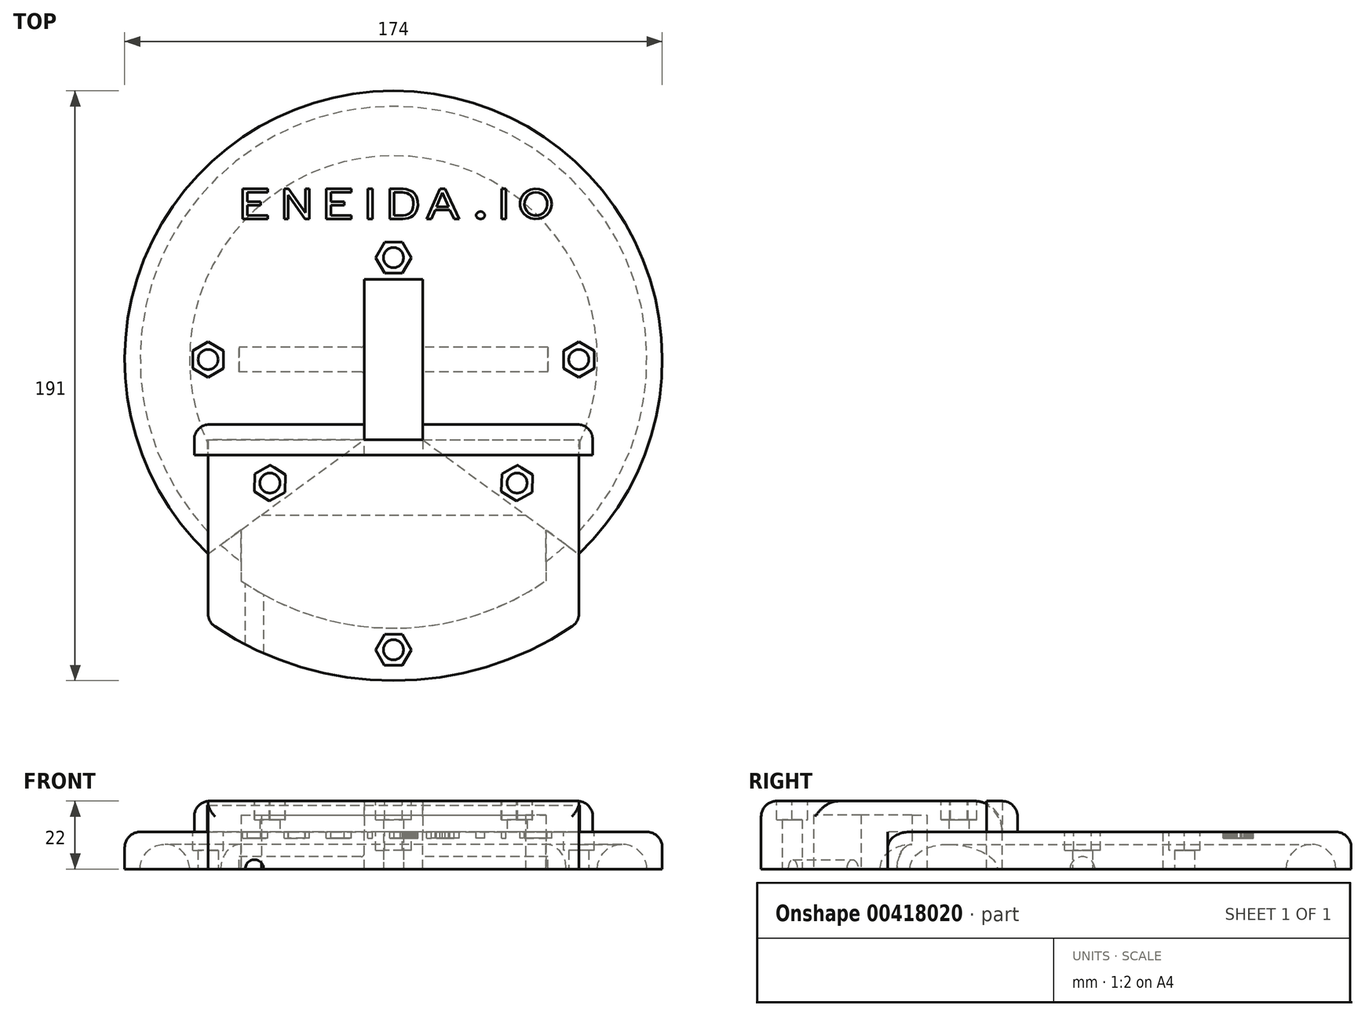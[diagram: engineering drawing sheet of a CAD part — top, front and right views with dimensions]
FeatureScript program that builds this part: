
annotation { "Feature Type Name" : "Feature", "Feature Type Description" : "" }
export const myFeature = defineFeature(function(context is Context, id is Id, definition is map)
    precondition{}
    {
        {
            var Q0;
            Q0=qCreatedBy(makeId("Top.planeOp"),FACE);
            var sketch = newSketch(context, id + "F0", { "sketchPlane" : qUnion([Q0])});
            skCircle(sketch, "E0", {"center": v(0, 0) * mm, "radius": 74 * mm});
            skCircle(sketch, "E1", {"center": v(0, 0) * mm, "radius": 87 * mm});
            skLineSegment(sketch, "E2", {"start": v(9.5, 26) * mm, "end": v(-9.5, 26) * mm});
            skLineSegment(sketch, "E3", {"start": v(-9.5, 26) * mm, "end": v(-9.5, -26) * mm});
            skLineSegment(sketch, "E4", {"start": v(9.5, 26) * mm, "end": v(9.5, -26) * mm});
            skCircle(sketch, "E5", {"center": v(-40, -40) * mm, "radius": 3.25 * mm});
            skCircle(sketch, "E6", {"center": v(-40, 40) * mm, "radius": 3.25 * mm});
            skCircle(sketch, "E7", {"center": v(40, 40) * mm, "radius": 3.25 * mm});
            skCircle(sketch, "E8", {"center": v(40, -40) * mm, "radius": 3.25 * mm});
            skPoint(sketch, "E9.endSnap0", {"position": v(0, 26) * mm});
            skCircle(sketch, "E10", {"center": v(0, 33) * mm, "radius": 3.25 * mm});
            skCircle(sketch, "E11", {"center": v(-60, 0) * mm, "radius": 3.25 * mm});
            skCircle(sketch, "E12", {"center": v(60, 0) * mm, "radius": 3.25 * mm});
            skLineSegment(sketch, "E13", {"start": v(0, 0) * mm, "end": v(-40, 0) * mm});
            skPoint(sketch, "E13.endSnap0", {"position": v(-9.5, 0) * mm});
            skLineSegment(sketch, "E14", {"start": v(-60, 0) * mm, "end": v(-60, -63) * mm});
            skLineSegment(sketch, "E15", {"start": v(-60, -63) * mm, "end": v(-9.5, -26) * mm});
            skLineSegment(sketch, "E16", {"start": v(60, 0) * mm, "end": v(60, -63) * mm});
            skLineSegment(sketch, "E17", {"start": v(60, -63) * mm, "end": v(9.5, -26) * mm});
            skLineSegment(sketch, "E18", {"start": v(-9.5, -26) * mm, "end": v(9.5, -26) * mm});
            skLineSegment(sketch, "E19", {"start": v(-9.5, -26) * mm, "end": v(-60, -26) * mm});
            skLineSegment(sketch, "E20", {"start": v(9.5, -26) * mm, "end": v(60, -26) * mm});
            skLineSegment(sketch, "E21", {"start": v(-42.7, -50.33) * mm, "end": v(42.7, -50.33) * mm});
            skLineSegment(sketch, "E22", {"start": v(-60, -63) * mm, "end": v(-60, -98) * mm});
            skCircle(sketch, "E23", {"center": v(0, 0) * mm, "radius": 114.9 * mm});
            skLineSegment(sketch, "E24", {"start": v(60, -63) * mm, "end": v(60, -98) * mm});
            skCircle(sketch, "E25", {"center": v(0, 0) * mm, "radius": 91 * mm});
            skLineSegment(sketch, "E26", {"start": v(-49.32, -55.17) * mm, "end": v(-49.32, -76.48) * mm});
            skLineSegment(sketch, "E27", {"start": v(49.32, -55.17) * mm, "end": v(49.32, -76.48) * mm});
            skLineSegment(sketch, "E28", {"start": v(0, 0) * mm, "end": v(0, -94) * mm});
            skCircle(sketch, "E29", {"center": v(0, -94) * mm, "radius": 3.25 * mm});
            skCircle(sketch, "E30", {"center": v(0, 0) * mm, "radius": 104 * mm});
            skLineSegment(sketch, "E31", {"start": v(-49.32, -76.48) * mm, "end": v(49.32, -76.48) * mm});
            skSolve(sketch);
        }
        {
            var Q0;
            {var subQ0=sQuery(id+"F0.wireOp",EDGE,"TgP18rpg-E85a-n0eO-8987-ISkSi9N6DLmr");var subQ1=sQuery(id+"F0.wireOp",EDGE,"E0");var subQ2=makeQuery(id+"F0.imprint","INTERSECT",VERTEX,{"derivedFrom":[subQ1,subQ0]});Q0=makeQuery(id+"F0.imprint","IMPRINT",FACE,{"disambiguationData":[TD([[makeQuery(id+"F0.imprint","IMPRINT",EDGE,{"disambiguationData":[TD([[subQ2,1.0]])],"derivedFrom":subQ1}),-1.0]])]});}
            var Q1;
            Q1=makeQuery(id+"F0.imprint","IMPRINT",FACE,{"disambiguationData":[TD([[makeQuery(id+"F0.imprint","IMPRINT",EDGE,{"derivedFrom":sQuery(id+"F0.wireOp",EDGE,"E2")}),-1.0]])]});
            var Q2;
            {var subQ0=sQuery(id+"F0.wireOp",EDGE,"RmQZDrMv-17gZ-rr8W-YuSi-1pivtKFGjAAM.left");var subQ1=sQuery(id+"F0.wireOp",EDGE,"RmQZDrMv-17gZ-rr8W-YuSi-1pivtKFGjAAM.bottom");var subQ2=makeQuery(id+"F0.imprint","INTERSECT",VERTEX,{"derivedFrom":[subQ1,subQ0]});Q2=makeQuery(id+"F0.imprint","IMPRINT",FACE,{"disambiguationData":[TD([[makeQuery(id+"F0.imprint","IMPRINT",EDGE,{"disambiguationData":[TD([[subQ2,-1.0]])],"derivedFrom":subQ1}),-1.0]])]});}
            var Q3;
            {var subQ0=sQuery(id+"F0.wireOp",EDGE,"RmQZDrMv-17gZ-rr8W-YuSi-1pivtKFGjAAM.left");var subQ1=sQuery(id+"F0.wireOp",EDGE,"RmQZDrMv-17gZ-rr8W-YuSi-1pivtKFGjAAM.bottom");var subQ2=makeQuery(id+"F0.imprint","INTERSECT",VERTEX,{"derivedFrom":[subQ1,subQ0]});Q3=makeQuery(id+"F0.imprint","IMPRINT",FACE,{"disambiguationData":[TD([[makeQuery(id+"F0.imprint","IMPRINT",EDGE,{"disambiguationData":[TD([[subQ2,-1.0]])],"derivedFrom":subQ1}),1.0]])]});}
            var Q4;
            {var subQ0=sQuery(id+"F0.wireOp",EDGE,"RmQZDrMv-17gZ-rr8W-YuSi-1pivtKFGjAAM.left");var subQ1=sQuery(id+"F0.wireOp",EDGE,"RmQZDrMv-17gZ-rr8W-YuSi-1pivtKFGjAAM.top");var subQ2=makeQuery(id+"F0.imprint","INTERSECT",VERTEX,{"derivedFrom":[subQ1,subQ0]});Q4=makeQuery(id+"F0.imprint","IMPRINT",FACE,{"disambiguationData":[TD([[makeQuery(id+"F0.imprint","IMPRINT",EDGE,{"disambiguationData":[TD([[subQ2,-1.0]])],"derivedFrom":subQ1}),1.0]])]});}
            var Q5;
            {var subQ0=sQuery(id+"F0.wireOp",EDGE,"RmQZDrMv-17gZ-rr8W-YuSi-1pivtKFGjAAM.left");var subQ1=sQuery(id+"F0.wireOp",EDGE,"RmQZDrMv-17gZ-rr8W-YuSi-1pivtKFGjAAM.top");var subQ2=makeQuery(id+"F0.imprint","INTERSECT",VERTEX,{"derivedFrom":[subQ1,subQ0]});Q5=makeQuery(id+"F0.imprint","IMPRINT",FACE,{"disambiguationData":[TD([[makeQuery(id+"F0.imprint","IMPRINT",EDGE,{"disambiguationData":[TD([[subQ2,-1.0]])],"derivedFrom":subQ1}),-1.0]])]});}
            var Q6;
            {var subQ0=sQuery(id+"F0.wireOp",EDGE,"RmQZDrMv-17gZ-rr8W-YuSi-1pivtKFGjAAM.right");var subQ1=sQuery(id+"F0.wireOp",EDGE,"RmQZDrMv-17gZ-rr8W-YuSi-1pivtKFGjAAM.top");var subQ2=makeQuery(id+"F0.imprint","INTERSECT",VERTEX,{"derivedFrom":[subQ1,subQ0]});Q6=makeQuery(id+"F0.imprint","IMPRINT",FACE,{"disambiguationData":[TD([[makeQuery(id+"F0.imprint","IMPRINT",EDGE,{"disambiguationData":[TD([[subQ2,1.0]])],"derivedFrom":subQ1}),1.0]])]});}
            var Q7;
            {var subQ0=sQuery(id+"F0.wireOp",EDGE,"RmQZDrMv-17gZ-rr8W-YuSi-1pivtKFGjAAM.right");var subQ1=sQuery(id+"F0.wireOp",EDGE,"RmQZDrMv-17gZ-rr8W-YuSi-1pivtKFGjAAM.top");var subQ2=makeQuery(id+"F0.imprint","INTERSECT",VERTEX,{"derivedFrom":[subQ1,subQ0]});Q7=makeQuery(id+"F0.imprint","IMPRINT",FACE,{"disambiguationData":[TD([[makeQuery(id+"F0.imprint","IMPRINT",EDGE,{"disambiguationData":[TD([[subQ2,1.0]])],"derivedFrom":subQ1}),-1.0]])]});}
            var Q8;
            {var subQ0=sQuery(id+"F0.wireOp",EDGE,"RmQZDrMv-17gZ-rr8W-YuSi-1pivtKFGjAAM.right");var subQ1=sQuery(id+"F0.wireOp",EDGE,"RmQZDrMv-17gZ-rr8W-YuSi-1pivtKFGjAAM.bottom");var subQ2=makeQuery(id+"F0.imprint","INTERSECT",VERTEX,{"derivedFrom":[subQ1,subQ0]});Q8=makeQuery(id+"F0.imprint","IMPRINT",FACE,{"disambiguationData":[TD([[makeQuery(id+"F0.imprint","IMPRINT",EDGE,{"disambiguationData":[TD([[subQ2,1.0]])],"derivedFrom":subQ1}),1.0]])]});}
            var Q9;
            {var subQ0=sQuery(id+"F0.wireOp",EDGE,"RmQZDrMv-17gZ-rr8W-YuSi-1pivtKFGjAAM.right");var subQ1=sQuery(id+"F0.wireOp",EDGE,"RmQZDrMv-17gZ-rr8W-YuSi-1pivtKFGjAAM.bottom");var subQ2=makeQuery(id+"F0.imprint","INTERSECT",VERTEX,{"derivedFrom":[subQ1,subQ0]});Q9=makeQuery(id+"F0.imprint","IMPRINT",FACE,{"disambiguationData":[TD([[makeQuery(id+"F0.imprint","IMPRINT",EDGE,{"disambiguationData":[TD([[subQ2,1.0]])],"derivedFrom":subQ1}),-1.0]])]});}
            var Q10;
            Q10=makeQuery(id+"F0.imprint","IMPRINT",FACE,{"disambiguationData":[TD([[makeQuery(id+"F0.imprint","IMPRINT",EDGE,{"derivedFrom":sQuery(id+"F0.wireOp",EDGE,"E7")}),1.0]])]});
            var Q11;
            Q11=makeQuery(id+"F0.imprint","IMPRINT",FACE,{"disambiguationData":[TD([[makeQuery(id+"F0.imprint","IMPRINT",EDGE,{"derivedFrom":sQuery(id+"F0.wireOp",EDGE,"E6")}),1.0]])]});
            var Q12;
            Q12=makeQuery(id+"F0.imprint","IMPRINT",FACE,{"disambiguationData":[TD([[makeQuery(id+"F0.imprint","IMPRINT",EDGE,{"derivedFrom":sQuery(id+"F0.wireOp",EDGE,"E5")}),1.0]])]});
            var Q13;
            Q13=makeQuery(id+"F0.imprint","IMPRINT",FACE,{"disambiguationData":[TD([[makeQuery(id+"F0.imprint","IMPRINT",EDGE,{"derivedFrom":sQuery(id+"F0.wireOp",EDGE,"E8")}),1.0]])]});
            var Q14;
            Q14=makeQuery(id+"F0.imprint","IMPRINT",FACE,{"disambiguationData":[TD([[makeQuery(id+"F0.imprint","IMPRINT",EDGE,{"derivedFrom":sQuery(id+"F0.wireOp",EDGE,"E8")}),-1.0]])]});
            var Q15;
            {var subQ0=sQuery(id+"F0.wireOp",EDGE,"E14");var subQ1=sQuery(id+"F0.wireOp",EDGE,"E0");var subQ2=makeQuery(id+"F0.imprint","INTERSECT",VERTEX,{"derivedFrom":[subQ1,subQ0]});Q15=makeQuery(id+"F0.imprint","IMPRINT",FACE,{"disambiguationData":[TD([[makeQuery(id+"F0.imprint","IMPRINT",EDGE,{"disambiguationData":[TD([[subQ2,1.0]])],"derivedFrom":subQ1}),-1.0]])]});}
            var Q16;
            Q16=makeQuery(id+"F0.imprint","IMPRINT",FACE,{"disambiguationData":[TD([[makeQuery(id+"F0.imprint","IMPRINT",EDGE,{"derivedFrom":sQuery(id+"F0.wireOp",EDGE,"E5")}),-1.0]])]});
            var Q17;
            {var subQ1=sQuery(id+"F0.wireOp",EDGE,"E0");var subQ3=sQuery(id+"F0.wireOp",EDGE,"E14");var subQ4=makeQuery(id+"F0.imprint","INTERSECT",VERTEX,{"derivedFrom":[subQ1,subQ3]});Q17=makeQuery(id+"F0.imprint","IMPRINT",FACE,{"disambiguationData":[TD([[makeQuery(id+"F0.imprint","IMPRINT",EDGE,{"disambiguationData":[TD([[subQ4,-1.0]])],"derivedFrom":subQ1}),-1.0]])]});}
            extrude(context, id + "F1", {"entities" : qUnion([Q0, Q1, Q2, Q3, Q4, Q5, Q6, Q7, Q8, Q9, Q10, Q11, Q12, Q13, Q14, Q15, Q16, Q17]), "depth" : 12 * mm});
        }
        {
            var Q0;
            Q0=makeQuery(id+"F0.imprint","IMPRINT",FACE,{"disambiguationData":[TD([[makeQuery(id+"F0.imprint","IMPRINT",EDGE,{"derivedFrom":sQuery(id+"F0.wireOp",EDGE,"E2")}),1.0]])]});
            var Q1;
            {var subQ0=sQuery(id+"F0.wireOp",EDGE,"TgP18rpg-E85a-n0eO-8987-ISkSi9N6DLmr");var subQ1=sQuery(id+"F0.wireOp",EDGE,"E0");var subQ2=makeQuery(id+"F0.imprint","INTERSECT",VERTEX,{"derivedFrom":[subQ1,subQ0]});Q1=makeQuery(id+"F0.imprint","IMPRINT",FACE,{"disambiguationData":[TD([[makeQuery(id+"F0.imprint","IMPRINT",EDGE,{"disambiguationData":[TD([[subQ2,-1.0]])],"derivedFrom":subQ1}),-1.0]])]});}
            extrude(context, id + "F2", {"entities" : qUnion([Q0, Q1]), "operationType" : NewBodyOperationType.REMOVE, "oppositeDirection" : true, "depth" : 12 * mm});
        }
        {
            var Q0;
            Q0=makeQuery(id+"F1.opExtrude","CAP_FACE",FACE,{"disambiguationData":[OSD([sQuery(id+"F0.wireOp",EDGE,"E1"),sQuery(id+"F0.wireOp",EDGE,"E2"),sQuery(id+"F0.wireOp",EDGE,"E3"),sQuery(id+"F0.wireOp",EDGE,"E4"),sQuery(id+"F0.wireOp",EDGE,"TgP18rpg-E85a-n0eO-8987-ISkSi9N6DLmr"),sQuery(id+"F0.wireOp",EDGE,"ek1SPQXI-mJC3-1PxT-7uTG-ug6Pz7o93UjJ"),sQuery(id+"F0.wireOp",EDGE,"E10"),sQuery(id+"F0.wireOp",EDGE,"E11"),sQuery(id+"F0.wireOp",EDGE,"E12")])],"isStart":false});
            cPlane(context, id + "F3", {"entities" : qUnion([Q0]), "cplaneType" : CPlaneType.OFFSET, "offset" : 0 * mm, "width" : 150 * mm, "height" : 150 * mm});
        }
        {
            var Q0;
            Q0=qCreatedBy(id+"F3.planeOp",FACE);
            var sketch = newSketch(context, id + "F4", { "sketchPlane" : qUnion([Q0])});
            skLineSegment(sketch, "E32", {"start": v(0, 0) * mm, "end": v(0, 33) * mm});
            skLineSegment(sketch, "E33.0", {"start": v(2.89, 28) * mm, "end": v(-2.89, 28) * mm});
            skLineSegment(sketch, "E33.1", {"start": v(-2.89, 28) * mm, "end": v(-5.77, 33) * mm});
            skLineSegment(sketch, "E33.2", {"start": v(-5.77, 33) * mm, "end": v(-2.89, 38) * mm});
            skLineSegment(sketch, "E33.3", {"start": v(-2.89, 38) * mm, "end": v(2.89, 38) * mm});
            skLineSegment(sketch, "E33.4", {"start": v(2.89, 38) * mm, "end": v(5.77, 33) * mm});
            skLineSegment(sketch, "E33.5", {"start": v(5.77, 33) * mm, "end": v(2.89, 28) * mm});
            skPoint(sketch, "E33.0.midPoint", {"position": v(0, 28) * mm});
            skLineSegment(sketch, "E34.0", {"start": v(-55, 2.89) * mm, "end": v(-55, -2.89) * mm});
            skLineSegment(sketch, "E34.1", {"start": v(-55, -2.89) * mm, "end": v(-60, -5.77) * mm});
            skLineSegment(sketch, "E34.2", {"start": v(-60, -5.77) * mm, "end": v(-65, -2.89) * mm});
            skLineSegment(sketch, "E34.3", {"start": v(-65, -2.89) * mm, "end": v(-65, 2.89) * mm});
            skLineSegment(sketch, "E34.4", {"start": v(-65, 2.89) * mm, "end": v(-60, 5.77) * mm});
            skLineSegment(sketch, "E34.5", {"start": v(-60, 5.77) * mm, "end": v(-55, 2.89) * mm});
            skPoint(sketch, "E34.0.midPoint", {"position": v(-55, 0) * mm});
            skLineSegment(sketch, "E35.0", {"start": v(55, -2.89) * mm, "end": v(55, 2.89) * mm});
            skLineSegment(sketch, "E35.1", {"start": v(55, 2.89) * mm, "end": v(60, 5.77) * mm});
            skLineSegment(sketch, "E35.2", {"start": v(60, 5.77) * mm, "end": v(65, 2.89) * mm});
            skLineSegment(sketch, "E35.3", {"start": v(65, 2.89) * mm, "end": v(65, -2.89) * mm});
            skLineSegment(sketch, "E35.4", {"start": v(65, -2.89) * mm, "end": v(60, -5.77) * mm});
            skLineSegment(sketch, "E35.5", {"start": v(60, -5.77) * mm, "end": v(55, -2.89) * mm});
            skPoint(sketch, "E35.0.midPoint", {"position": v(55, 0) * mm});
            skLineSegment(sketch, "E36", {"start": v(-40.73, 46.64) * mm, "end": v(-40.73, 45.51) * mm});
            skLineSegment(sketch, "E37", {"start": v(-40.73, 45.51) * mm, "end": v(-48.83, 45.51) * mm});
            skLineSegment(sketch, "E38", {"start": v(-48.83, 45.51) * mm, "end": v(-48.83, 55.3) * mm});
            skLineSegment(sketch, "E39", {"start": v(-48.83, 55.3) * mm, "end": v(-40.73, 55.3) * mm});
            skLineSegment(sketch, "E40", {"start": v(-40.73, 55.3) * mm, "end": v(-40.73, 54.18) * mm});
            skLineSegment(sketch, "E41", {"start": v(-40.73, 54.18) * mm, "end": v(-47.36, 54.18) * mm});
            skLineSegment(sketch, "E42", {"start": v(-47.36, 54.18) * mm, "end": v(-47.36, 51.15) * mm});
            skLineSegment(sketch, "E43", {"start": v(-47.36, 51.15) * mm, "end": v(-42.98, 51.15) * mm});
            skLineSegment(sketch, "E44", {"start": v(-42.98, 51.15) * mm, "end": v(-42.98, 49.95) * mm});
            skLineSegment(sketch, "E45", {"start": v(-42.98, 49.95) * mm, "end": v(-47.36, 49.95) * mm});
            skLineSegment(sketch, "E46", {"start": v(-40.73, 46.64) * mm, "end": v(-47.36, 46.64) * mm});
            skLineSegment(sketch, "E47", {"start": v(-47.36, 49.95) * mm, "end": v(-47.36, 46.64) * mm});
            skLineSegment(sketch, "E48", {"start": v(-35.33, 55.3) * mm, "end": v(-35.33, 45.51) * mm});
            skLineSegment(sketch, "E49", {"start": v(-34.04, 45.51) * mm, "end": v(-34.04, 53.24) * mm});
            skLineSegment(sketch, "E50", {"start": v(-35.33, 45.51) * mm, "end": v(-34.04, 45.51) * mm});
            skLineSegment(sketch, "E51", {"start": v(-27.25, 55.3) * mm, "end": v(-27.25, 45.51) * mm});
            skLineSegment(sketch, "E52", {"start": v(-28.53, 55.3) * mm, "end": v(-28.53, 47.57) * mm});
            skLineSegment(sketch, "E53", {"start": v(-27.25, 55.3) * mm, "end": v(-28.53, 55.3) * mm});
            skLineSegment(sketch, "E54", {"start": v(-27.25, 45.51) * mm, "end": v(-28.65, 45.51) * mm});
            skLineSegment(sketch, "E55", {"start": v(-34.04, 53.24) * mm, "end": v(-28.65, 45.51) * mm});
            skLineSegment(sketch, "E56", {"start": v(-35.33, 55.3) * mm, "end": v(-33.92, 55.3) * mm});
            skLineSegment(sketch, "E57", {"start": v(-28.53, 47.57) * mm, "end": v(-33.92, 55.3) * mm});
            skLineSegment(sketch, "E58", {"start": v(-13.67, 46.64) * mm, "end": v(-13.67, 45.51) * mm});
            skLineSegment(sketch, "E59", {"start": v(-13.67, 45.51) * mm, "end": v(-21.77, 45.51) * mm});
            skLineSegment(sketch, "E60", {"start": v(-21.77, 45.51) * mm, "end": v(-21.77, 55.3) * mm});
            skLineSegment(sketch, "E61", {"start": v(-21.77, 55.3) * mm, "end": v(-13.67, 55.3) * mm});
            skLineSegment(sketch, "E62", {"start": v(-13.67, 55.3) * mm, "end": v(-13.67, 54.18) * mm});
            skLineSegment(sketch, "E63", {"start": v(-13.67, 54.18) * mm, "end": v(-20.3, 54.18) * mm});
            skLineSegment(sketch, "E64", {"start": v(-20.3, 54.18) * mm, "end": v(-20.3, 51.15) * mm});
            skLineSegment(sketch, "E65", {"start": v(-20.3, 51.15) * mm, "end": v(-15.91, 51.15) * mm});
            skLineSegment(sketch, "E66", {"start": v(-15.91, 51.15) * mm, "end": v(-15.91, 49.95) * mm});
            skLineSegment(sketch, "E67", {"start": v(-15.91, 49.95) * mm, "end": v(-20.3, 49.95) * mm});
            skLineSegment(sketch, "E68", {"start": v(-13.67, 46.64) * mm, "end": v(-20.3, 46.64) * mm});
            skLineSegment(sketch, "E69", {"start": v(-20.3, 49.95) * mm, "end": v(-20.3, 46.64) * mm});
            skLineSegment(sketch, "E70", {"start": v(-8.25, 55.3) * mm, "end": v(-8.25, 45.51) * mm});
            skLineSegment(sketch, "E71", {"start": v(-6.8, 55.3) * mm, "end": v(-6.8, 45.51) * mm});
            skLineSegment(sketch, "E72", {"start": v(-8.25, 55.3) * mm, "end": v(-6.8, 55.3) * mm});
            skLineSegment(sketch, "E73", {"start": v(-8.25, 45.51) * mm, "end": v(-6.8, 45.51) * mm});
            skLineSegment(sketch, "E74", {"start": v(34.95, 55.3) * mm, "end": v(34.95, 45.51) * mm});
            skLineSegment(sketch, "E75", {"start": v(36.41, 55.3) * mm, "end": v(36.41, 45.51) * mm});
            skLineSegment(sketch, "E76", {"start": v(34.95, 55.3) * mm, "end": v(36.41, 55.3) * mm});
            skLineSegment(sketch, "E77", {"start": v(34.95, 45.51) * mm, "end": v(36.41, 45.51) * mm});
            skLineSegment(sketch, "E78", {"start": v(10.68, 45.51) * mm, "end": v(12.28, 45.51) * mm});
            skLineSegment(sketch, "E79", {"start": v(15.02, 55.3) * mm, "end": v(16.66, 55.3) * mm});
            skLineSegment(sketch, "E80", {"start": v(15.02, 55.3) * mm, "end": v(10.68, 45.51) * mm});
            skLineSegment(sketch, "E81", {"start": v(16.66, 55.3) * mm, "end": v(21.31, 45.51) * mm});
            skLineSegment(sketch, "E82", {"start": v(21.31, 45.51) * mm, "end": v(19.59, 45.51) * mm});
            skLineSegment(sketch, "E83", {"start": v(19.59, 45.51) * mm, "end": v(18.29, 48.48) * mm});
            skLineSegment(sketch, "E84", {"start": v(18.29, 48.48) * mm, "end": v(13.55, 48.48) * mm});
            skLineSegment(sketch, "E85", {"start": v(13.55, 48.48) * mm, "end": v(12.28, 45.51) * mm});
            skLineSegment(sketch, "E86", {"start": v(13.94, 49.51) * mm, "end": v(15.81, 54.03) * mm});
            skLineSegment(sketch, "E87", {"start": v(15.81, 54.03) * mm, "end": v(17.84, 49.52) * mm});
            skLineSegment(sketch, "E88", {"start": v(17.84, 49.52) * mm, "end": v(13.94, 49.51) * mm});
            skEllipse(sketch, "E89", {"center": v(28.16, 46.7) * mm, "majorRadius": 1.38 * mm, "minorRadius": 1.2 * mm, "majorAxis": v(1, 0)});
            skEllipse(sketch, "E90", {"center": v(46.1, 50.4) * mm, "majorRadius": 5.13 * mm, "minorRadius": 4.9 * mm, "majorAxis": v(1, 0)});
            skEllipse(sketch, "E91", {"center": v(46.1, 50.4) * mm, "majorRadius": 3.8 * mm, "minorRadius": 3.68 * mm, "majorAxis": v(0, 1)});
            skLineSegment(sketch, "E92", {"start": v(-1.22, 55.3) * mm, "end": v(-1.22, 45.51) * mm});
            skLineSegment(sketch, "E93", {"start": v(-1.22, 45.51) * mm, "end": v(2.27, 45.51) * mm});
            skLineSegment(sketch, "E94", {"start": v(2.27, 45.51) * mm, "end": v(2.99, 45.53) * mm});
            skLineSegment(sketch, "E95", {"start": v(2.99, 45.53) * mm, "end": v(3.9, 45.62) * mm});
            skLineSegment(sketch, "E96", {"start": v(3.9, 45.62) * mm, "end": v(4.74, 45.83) * mm});
            skLineSegment(sketch, "E97", {"start": v(4.74, 45.83) * mm, "end": v(5.68, 46.18) * mm});
            skLineSegment(sketch, "E98", {"start": v(5.68, 46.18) * mm, "end": v(6.31, 46.56) * mm});
            skLineSegment(sketch, "E99", {"start": v(6.31, 46.56) * mm, "end": v(6.84, 47.07) * mm});
            skLineSegment(sketch, "E100", {"start": v(6.84, 47.07) * mm, "end": v(7.34, 47.77) * mm});
            skLineSegment(sketch, "E101", {"start": v(7.34, 47.77) * mm, "end": v(7.75, 48.82) * mm});
            skLineSegment(sketch, "E102", {"start": v(7.75, 48.82) * mm, "end": v(7.92, 50) * mm});
            skLineSegment(sketch, "E103", {"start": v(7.92, 50) * mm, "end": v(7.87, 51.26) * mm});
            skLineSegment(sketch, "E104", {"start": v(7.87, 51.26) * mm, "end": v(7.63, 52.4) * mm});
            skLineSegment(sketch, "E105", {"start": v(7.63, 52.4) * mm, "end": v(7.2, 53.29) * mm});
            skLineSegment(sketch, "E106", {"start": v(7.2, 53.29) * mm, "end": v(6.67, 53.93) * mm});
            skLineSegment(sketch, "E107", {"start": v(6.67, 53.93) * mm, "end": v(6.11, 54.38) * mm});
            skLineSegment(sketch, "E108", {"start": v(6.11, 54.38) * mm, "end": v(5.17, 54.84) * mm});
            skLineSegment(sketch, "E109", {"start": v(5.17, 54.84) * mm, "end": v(4.2, 55.12) * mm});
            skLineSegment(sketch, "E110", {"start": v(4.2, 55.12) * mm, "end": v(3.1, 55.26) * mm});
            skLineSegment(sketch, "E111", {"start": v(3.1, 55.26) * mm, "end": v(2.19, 55.3) * mm});
            skLineSegment(sketch, "E112", {"start": v(2.19, 55.3) * mm, "end": v(-1.22, 55.3) * mm});
            skLineSegment(sketch, "E113", {"start": v(0.24, 54.13) * mm, "end": v(0.24, 46.68) * mm});
            skLineSegment(sketch, "E114", {"start": v(0.24, 46.68) * mm, "end": v(2.92, 46.68) * mm});
            skLineSegment(sketch, "E115", {"start": v(2.92, 46.68) * mm, "end": v(3.27, 46.7) * mm});
            skLineSegment(sketch, "E116", {"start": v(3.27, 46.7) * mm, "end": v(4.04, 46.85) * mm});
            skLineSegment(sketch, "E117", {"start": v(4.04, 46.85) * mm, "end": v(4.59, 47) * mm});
            skLineSegment(sketch, "E118", {"start": v(4.59, 47) * mm, "end": v(5.16, 47.33) * mm});
            skLineSegment(sketch, "E119", {"start": v(5.16, 47.33) * mm, "end": v(5.57, 47.68) * mm});
            skLineSegment(sketch, "E120", {"start": v(5.57, 47.68) * mm, "end": v(5.85, 48) * mm});
            skLineSegment(sketch, "E121", {"start": v(5.85, 48) * mm, "end": v(6.17, 48.66) * mm});
            skLineSegment(sketch, "E122", {"start": v(6.17, 48.66) * mm, "end": v(6.34, 49.32) * mm});
            skLineSegment(sketch, "E123", {"start": v(6.34, 49.32) * mm, "end": v(6.4, 50.15) * mm});
            skLineSegment(sketch, "E124", {"start": v(6.4, 50.15) * mm, "end": v(6.38, 51.1) * mm});
            skLineSegment(sketch, "E125", {"start": v(6.38, 51.1) * mm, "end": v(6.3, 51.7) * mm});
            skLineSegment(sketch, "E126", {"start": v(6.3, 51.7) * mm, "end": v(6.12, 52.33) * mm});
            skLineSegment(sketch, "E127", {"start": v(6.12, 52.33) * mm, "end": v(5.85, 52.82) * mm});
            skLineSegment(sketch, "E128", {"start": v(5.85, 52.82) * mm, "end": v(5.58, 53.13) * mm});
            skLineSegment(sketch, "E129", {"start": v(5.58, 53.13) * mm, "end": v(5.06, 53.55) * mm});
            skLineSegment(sketch, "E130", {"start": v(5.06, 53.55) * mm, "end": v(4.34, 53.87) * mm});
            skLineSegment(sketch, "E131", {"start": v(4.34, 53.87) * mm, "end": v(3.53, 54.06) * mm});
            skLineSegment(sketch, "E132", {"start": v(3.53, 54.06) * mm, "end": v(2.83, 54.13) * mm});
            skLineSegment(sketch, "E133", {"start": v(2.83, 54.13) * mm, "end": v(0.24, 54.13) * mm});
            skLineSegment(sketch, "E134", {"start": v(0, 0) * mm, "end": v(0, -31) * mm});
            skLineSegment(sketch, "E135", {"start": v(0, -31) * mm, "end": v(9.5, -31) * mm});
            skLineSegment(sketch, "E136", {"start": v(0, -31) * mm, "end": v(-9.5, -31) * mm});
            skLineSegment(sketch, "E137", {"start": v(-9.5, -31) * mm, "end": v(-64.5, -31) * mm});
            skLineSegment(sketch, "E138", {"start": v(9.5, -31) * mm, "end": v(64.5, -31) * mm});
            skLineSegment(sketch, "E139", {"start": v(-9.5, -31) * mm, "end": v(-9.5, -21) * mm});
            skLineSegment(sketch, "E140", {"start": v(-9.5, -21) * mm, "end": v(-64.5, -21) * mm});
            skLineSegment(sketch, "E141", {"start": v(-64.5, -21) * mm, "end": v(-64.5, -31) * mm});
            skLineSegment(sketch, "E142", {"start": v(64.5, -31) * mm, "end": v(64.5, -21) * mm});
            skLineSegment(sketch, "E143", {"start": v(64.5, -21) * mm, "end": v(9.5, -21) * mm});
            skLineSegment(sketch, "E144", {"start": v(9.5, -21) * mm, "end": v(9.5, -31) * mm});
            skLineSegment(sketch, "E145", {"start": v(0, -31) * mm, "end": v(0, -26) * mm});
            skLineSegment(sketch, "E146", {"start": v(0, -26) * mm, "end": v(60, -26) * mm});
            skLineSegment(sketch, "E147", {"start": v(0, -26) * mm, "end": v(-60, -26) * mm});
            skCircle(sketch, "E148", {"center": v(0, 0) * mm, "radius": 87 * mm});
            skLineSegment(sketch, "E149", {"start": v(-60, -26) * mm, "end": v(-60, -63) * mm});
            skLineSegment(sketch, "E150", {"start": v(60, -26) * mm, "end": v(60, -63) * mm});
            skLineSegment(sketch, "E151", {"start": v(-60, -63) * mm, "end": v(-9.5, -26) * mm});
            skLineSegment(sketch, "E152", {"start": v(-9.5, -26) * mm, "end": v(9.5, -26) * mm});
            skLineSegment(sketch, "E153", {"start": v(9.5, -26) * mm, "end": v(60, -63) * mm});
            skSolve(sketch);
        }
        {
            var Q0;
            {var subQ0=sQuery(id+"F4.wireOp",EDGE,"E33.1");Q0=makeQuery(id+"F4.imprint","IMPRINT",FACE,{"disambiguationData":[TD([[makeQuery(id+"F4.imprint","IMPRINT",EDGE,{"derivedFrom":subQ0}),-1.0]])]});}
            var Q1;
            {var subQ0=sQuery(id+"F4.wireOp",EDGE,"E35.1");Q1=makeQuery(id+"F4.imprint","IMPRINT",FACE,{"disambiguationData":[TD([[makeQuery(id+"F4.imprint","IMPRINT",EDGE,{"derivedFrom":subQ0}),-1.0]])]});}
            var Q2;
            {var subQ0=sQuery(id+"F4.wireOp",EDGE,"E34.1");Q2=makeQuery(id+"F4.imprint","IMPRINT",FACE,{"disambiguationData":[TD([[makeQuery(id+"F4.imprint","IMPRINT",EDGE,{"derivedFrom":subQ0}),-1.0]])]});}
            extrude(context, id + "F5", {"entities" : qUnion([Q0, Q1, Q2]), "operationType" : NewBodyOperationType.REMOVE, "oppositeDirection" : true, "depth" : 6 * mm});
        }
        {
            var Q0;
            Q0=makeQuery(id+"F1.opExtrude","CAP_EDGE",EDGE,{"disambiguationData":[OSD([sQuery(id+"F0.wireOp",EDGE,"E1")])],"isStart":false});
            fillet(context, id + "F6", {"entities" : qUnion([Q0]), "radius" : 5 * mm, "tangentPropagation" : true, "allowEdgeOverflow" : false});
        }
        {
            var Q0;
            Q0=qCreatedBy(makeId("Right.planeOp"),FACE);
            cPlane(context, id + "F7", {"entities" : qUnion([Q0]), "cplaneType" : CPlaneType.OFFSET, "offset" : 50 * mm, "oppositeDirection" : true, "width" : 150 * mm, "height" : 150 * mm});
        }
        {
            var Q0;
            Q0=qCreatedBy(id+"F7.planeOp",FACE);
            var sketch = newSketch(context, id + "F8", { "sketchPlane" : qUnion([Q0])});
            skCircle(sketch, "E154", {"center": v(0, 0) * mm, "radius": 4 * mm});
            skSolve(sketch);
        }
        {
            var Q0;
            Q0=makeQuery(id+"F8.imprint","IMPRINT",FACE,{"disambiguationData":[TD([[makeQuery(id+"F8.imprint","IMPRINT",EDGE,{"derivedFrom":sQuery(id+"F8.wireOp",EDGE,"E154")}),1.0]])]});
            extrude(context, id + "F9", {"entities" : qUnion([Q0]), "operationType" : NewBodyOperationType.REMOVE, "depth" : 100 * mm});
        }
        {
            var Q0;
            Q0=makeQuery(id+"F4.imprint","IMPRINT",FACE,{"disambiguationData":[TD([[makeQuery(id+"F4.imprint","IMPRINT",EDGE,{"derivedFrom":sQuery(id+"F4.wireOp",EDGE,"E90")}),1.0]])]});
            var Q1;
            Q1=makeQuery(id+"F4.imprint","IMPRINT",FACE,{"disambiguationData":[TD([[makeQuery(id+"F4.imprint","IMPRINT",EDGE,{"derivedFrom":sQuery(id+"F4.wireOp",EDGE,"E74")}),1.0]])]});
            var Q2;
            Q2=makeQuery(id+"F4.imprint","IMPRINT",FACE,{"disambiguationData":[TD([[makeQuery(id+"F4.imprint","IMPRINT",EDGE,{"derivedFrom":sQuery(id+"F4.wireOp",EDGE,"E89")}),1.0]])]});
            var Q3;
            Q3=makeQuery(id+"F4.imprint","IMPRINT",FACE,{"disambiguationData":[TD([[makeQuery(id+"F4.imprint","IMPRINT",EDGE,{"derivedFrom":sQuery(id+"F4.wireOp",EDGE,"E78")}),1.0]])]});
            var Q4;
            Q4=makeQuery(id+"F4.imprint","IMPRINT",FACE,{"disambiguationData":[TD([[makeQuery(id+"F4.imprint","IMPRINT",EDGE,{"derivedFrom":sQuery(id+"F4.wireOp",EDGE,"E92")}),1.0]])]});
            var Q5;
            Q5=makeQuery(id+"F4.imprint","IMPRINT",FACE,{"disambiguationData":[TD([[makeQuery(id+"F4.imprint","IMPRINT",EDGE,{"derivedFrom":sQuery(id+"F4.wireOp",EDGE,"E36")}),-1.0]])]});
            var Q6;
            Q6=makeQuery(id+"F4.imprint","IMPRINT",FACE,{"disambiguationData":[TD([[makeQuery(id+"F4.imprint","IMPRINT",EDGE,{"derivedFrom":sQuery(id+"F4.wireOp",EDGE,"E48")}),1.0]])]});
            var Q7;
            Q7=makeQuery(id+"F4.imprint","IMPRINT",FACE,{"disambiguationData":[TD([[makeQuery(id+"F4.imprint","IMPRINT",EDGE,{"derivedFrom":sQuery(id+"F4.wireOp",EDGE,"E58")}),-1.0]])]});
            var Q8;
            Q8=makeQuery(id+"F4.imprint","IMPRINT",FACE,{"disambiguationData":[TD([[makeQuery(id+"F4.imprint","IMPRINT",EDGE,{"derivedFrom":sQuery(id+"F4.wireOp",EDGE,"E70")}),1.0]])]});
            extrude(context, id + "F10", {"entities" : qUnion([Q0, Q1, Q2, Q3, Q4, Q5, Q6, Q7, Q8]), "operationType" : NewBodyOperationType.REMOVE, "oppositeDirection" : true, "depth" : 2 * mm});
        }
        {
            var Q0;
            Q0=makeQuery(id+"F0.imprint","IMPRINT",FACE,{"disambiguationData":[TD([[makeQuery(id+"F0.imprint","IMPRINT",EDGE,{"derivedFrom":sQuery(id+"F0.wireOp",EDGE,"E5")}),1.0]])]});
            var Q1;
            Q1=makeQuery(id+"F0.imprint","IMPRINT",FACE,{"disambiguationData":[TD([[makeQuery(id+"F0.imprint","IMPRINT",EDGE,{"derivedFrom":sQuery(id+"F0.wireOp",EDGE,"E8")}),1.0]])]});
            extrude(context, id + "F11", {"entities" : qUnion([Q0, Q1]), "operationType" : NewBodyOperationType.REMOVE, "depth" : 12 * mm});
        }
        {
            var Q0;
            Q0=makeQuery(id+"F4.imprint","IMPRINT",FACE,{"disambiguationData":[TD([[makeQuery(id+"F4.imprint","IMPRINT",EDGE,{"derivedFrom":sQuery(id+"F4.wireOp",EDGE,"E137")}),-1.0]])]});
            var Q1;
            Q1=makeQuery(id+"F4.imprint","IMPRINT",FACE,{"disambiguationData":[TD([[makeQuery(id+"F4.imprint","IMPRINT",EDGE,{"derivedFrom":sQuery(id+"F4.wireOp",EDGE,"E138")}),1.0]])]});
            var Q2;
            {var subQ1=sQuery(id+"F4.wireOp",EDGE,"E140");Q2=makeQuery(id+"F4.imprint","IMPRINT",FACE,{"disambiguationData":[TD([[makeQuery(id+"F4.imprint","IMPRINT",EDGE,{"derivedFrom":subQ1}),1.0]])]});}
            var Q3;
            {var subQ8=sQuery(id+"F4.wireOp",EDGE,"E142");Q3=makeQuery(id+"F4.imprint","IMPRINT",FACE,{"disambiguationData":[TD([[makeQuery(id+"F4.imprint","IMPRINT",EDGE,{"derivedFrom":subQ8}),1.0]])]});}
            var Q4;
            {var subQ5=sQuery(id+"F4.wireOp",EDGE,"E146");Q4=makeQuery(id+"F4.imprint","IMPRINT",FACE,{"disambiguationData":[TD([[makeQuery(id+"F4.imprint","IMPRINT",EDGE,{"derivedFrom":subQ5}),-1.0]])]});}
            var Q5;
            {var subQ5=sQuery(id+"F4.wireOp",EDGE,"E147");Q5=makeQuery(id+"F4.imprint","IMPRINT",FACE,{"disambiguationData":[TD([[makeQuery(id+"F4.imprint","IMPRINT",EDGE,{"derivedFrom":subQ5}),1.0]])]});}
            extrude(context, id + "F12", {"entities" : qUnion([Q0, Q1, Q2, Q3, Q4, Q5]), "operationType" : NewBodyOperationType.ADD, "depth" : (10) * mm});
        }
        {
            var Q0;
            Q0=makeQuery(id+"F12.opExtrude","CAP_EDGE",EDGE,{"disambiguationData":[OSD([sQuery(id+"F4.wireOp",EDGE,"E140")])],"isStart":false});
            var Q1;
            Q1=makeQuery(id+"F12.opExtrude","CAP_EDGE",EDGE,{"disambiguationData":[OSD([sQuery(id+"F4.wireOp",EDGE,"E143")])],"isStart":false});
            fillet(context, id + "F13", {"entities" : qUnion([Q0, Q1]), "radius" : 5 * mm, "tangentPropagation" : true, "allowEdgeOverflow" : false});
        }
        {
            var Q0;
            Q0=qCreatedBy(makeId("Right.planeOp"),FACE);
            var sketch = newSketch(context, id + "F14", { "sketchPlane" : qUnion([Q0])});
            skLineSegment(sketch, "E155", {"start": v(0, 0) * mm, "end": v(-31, 0) * mm});
            skLineSegment(sketch, "E156", {"start": v(-31, 0) * mm, "end": v(-31, 12) * mm});
            skLineSegment(sketch, "E157", {"start": v(-31, 12) * mm, "end": v(-36, 12) * mm});
            skCircle(sketch, "E158", {"center": v(-36, 12) * mm, "radius": 10 * mm});
            skLineSegment(sketch, "E159", {"start": v(-36, 12) * mm, "end": v(-36, 22) * mm});
            skLineSegment(sketch, "E160", {"start": v(-31, 12) * mm, "end": v(-26, 12) * mm});
            skSolve(sketch);
        }
        {
            var Q0;
            Q0=makeQuery(id+"F14.imprint","IMPRINT",FACE,{"disambiguationData":[TD([[makeQuery(id+"F14.imprint","IMPRINT",EDGE,{"derivedFrom":sQuery(id+"F14.wireOp",EDGE,"E157")}),-1.0]])]});
            extrude(context, id + "F15", {"entities" : qUnion([Q0]), "operationType" : NewBodyOperationType.REMOVE, "endBound" : BoundingType.SYMMETRIC, "oppositeDirection" : true, "depth" : 120.5 * mm});
        }
        {
            var Q0;
            Q0=makeQuery(id+"F12.opExtrude","SWEPT_EDGE",EDGE,{"disambiguationData":[OSD([sQuery(id+"F4.wireOp",EDGE,"E142"),sQuery(id+"F4.wireOp",EDGE,"E143")])]});
            var Q1;
            Q1=makeQuery(id+"F13.opFillet","BLEND_EDGE",EDGE,{"blendedFrom":[makeQuery(id+"F12.opExtrude","CAP_EDGE",EDGE,{"disambiguationData":[OSD([sQuery(id+"F4.wireOp",EDGE,"E143")])],"isStart":false}),makeQuery(id+"F12.opExtrude","SWEPT_FACE",FACE,{"disambiguationData":[OSD([sQuery(id+"F4.wireOp",EDGE,"E142")])]})],"blendedInto":[makeQuery(id+"F12.opExtrude","SWEPT_FACE",FACE,{"disambiguationData":[OSD([sQuery(id+"F4.wireOp",EDGE,"E142")])]})]});
            var Q2;
            Q2=makeQuery(id+"F12.opExtrude","CAP_EDGE",EDGE,{"disambiguationData":[OSD([sQuery(id+"F4.wireOp",EDGE,"E142")])],"isStart":false});
            var Q3;
            Q3=makeQuery(id+"F12.opExtrude","SWEPT_EDGE",EDGE,{"disambiguationData":[OSD([sQuery(id+"F4.wireOp",EDGE,"E140"),sQuery(id+"F4.wireOp",EDGE,"E141")])]});
            var Q4;
            Q4=makeQuery(id+"F13.opFillet","BLEND_EDGE",EDGE,{"blendedFrom":[makeQuery(id+"F12.opExtrude","CAP_EDGE",EDGE,{"disambiguationData":[OSD([sQuery(id+"F4.wireOp",EDGE,"E140")])],"isStart":false}),makeQuery(id+"F12.opExtrude","SWEPT_FACE",FACE,{"disambiguationData":[OSD([sQuery(id+"F4.wireOp",EDGE,"E141")])]})],"blendedInto":[makeQuery(id+"F12.opExtrude","SWEPT_FACE",FACE,{"disambiguationData":[OSD([sQuery(id+"F4.wireOp",EDGE,"E141")])]})]});
            var Q5;
            Q5=makeQuery(id+"F12.opExtrude","CAP_EDGE",EDGE,{"disambiguationData":[OSD([sQuery(id+"F4.wireOp",EDGE,"E141")])],"isStart":false});
            fillet(context, id + "F16", {"entities" : qUnion([Q0, Q1, Q2, Q3, Q4, Q5]), "radius" : 5 * mm, "tangentPropagation" : true, "allowEdgeOverflow" : false});
        }
        {
            var Q0;
            {var subQ0=sQuery(id+"F0.wireOp",EDGE,"E28");var subQ1=sQuery(id+"F0.wireOp",EDGE,"E1");var subQ2=makeQuery(id+"F0.imprint","INTERSECT",VERTEX,{"derivedFrom":[subQ1,subQ0]});Q0=makeQuery(id+"F0.imprint","IMPRINT",FACE,{"disambiguationData":[TD([[makeQuery(id+"F0.imprint","IMPRINT",EDGE,{"disambiguationData":[TD([[subQ2,-1.0]])],"derivedFrom":subQ1}),-1.0]])]});}
            var Q1;
            {var subQ3=sQuery(id+"F0.wireOp",EDGE,"E26");var subQ5=sQuery(id+"F0.wireOp",EDGE,"E25");var subQ7=makeQuery(id+"F0.imprint","INTERSECT",VERTEX,{"derivedFrom":[subQ5,subQ3]});Q1=makeQuery(id+"F0.imprint","IMPRINT",FACE,{"disambiguationData":[TD([[makeQuery(id+"F0.imprint","IMPRINT",EDGE,{"disambiguationData":[TD([[subQ7,1.0]])],"derivedFrom":subQ5}),1.0]])]});}
            var Q2;
            {var subQ1=sQuery(id+"F0.wireOp",EDGE,"E15");var subQ3=sQuery(id+"F0.wireOp",EDGE,"E21");var subQ4=makeQuery(id+"F0.imprint","INTERSECT",VERTEX,{"derivedFrom":[subQ1,subQ3]});Q2=makeQuery(id+"F0.imprint","IMPRINT",FACE,{"disambiguationData":[TD([[makeQuery(id+"F0.imprint","IMPRINT",EDGE,{"disambiguationData":[TD([[subQ4,-1.0]])],"derivedFrom":subQ3}),1.0]])]});}
            var Q3;
            {var subQ0=sQuery(id+"F0.wireOp",EDGE,"E26");var subQ5=sQuery(id+"F0.wireOp",EDGE,"E1");var subQ6=makeQuery(id+"F0.imprint","INTERSECT",VERTEX,{"derivedFrom":[subQ5,subQ0]});Q3=makeQuery(id+"F0.imprint","IMPRINT",FACE,{"disambiguationData":[TD([[makeQuery(id+"F0.imprint","IMPRINT",EDGE,{"disambiguationData":[TD([[subQ6,-1.0]])],"derivedFrom":subQ5}),1.0]])]});}
            var Q4;
            Q4=makeQuery(id+"F0.imprint","IMPRINT",FACE,{"disambiguationData":[TD([[makeQuery(id+"F0.imprint","IMPRINT",EDGE,{"derivedFrom":sQuery(id+"F0.wireOp",EDGE,"E5")}),-1.0]])]});
            var Q5;
            {var subQ1=sQuery(id+"F0.wireOp",EDGE,"E0");var subQ3=sQuery(id+"F0.wireOp",EDGE,"E14");var subQ4=makeQuery(id+"F0.imprint","INTERSECT",VERTEX,{"derivedFrom":[subQ1,subQ3]});Q5=makeQuery(id+"F0.imprint","IMPRINT",FACE,{"disambiguationData":[TD([[makeQuery(id+"F0.imprint","IMPRINT",EDGE,{"disambiguationData":[TD([[subQ4,-1.0]])],"derivedFrom":subQ1}),-1.0]])]});}
            var Q6;
            Q6=makeQuery(id+"F0.imprint","IMPRINT",FACE,{"disambiguationData":[TD([[makeQuery(id+"F0.imprint","IMPRINT",EDGE,{"derivedFrom":sQuery(id+"F0.wireOp",EDGE,"E8")}),-1.0]])]});
            var Q7;
            {var subQ1=sQuery(id+"F0.wireOp",EDGE,"E0");var subQ3=sQuery(id+"F0.wireOp",EDGE,"E16");var subQ4=makeQuery(id+"F0.imprint","INTERSECT",VERTEX,{"derivedFrom":[subQ1,subQ3]});Q7=makeQuery(id+"F0.imprint","IMPRINT",FACE,{"disambiguationData":[TD([[makeQuery(id+"F0.imprint","IMPRINT",EDGE,{"disambiguationData":[TD([[subQ4,1.0]])],"derivedFrom":subQ1}),-1.0]])]});}
            var Q8;
            {var subQ0=sQuery(id+"F0.wireOp",EDGE,"E15");var subQ5=sQuery(id+"F0.wireOp",EDGE,"E21");var subQ6=makeQuery(id+"F0.imprint","INTERSECT",VERTEX,{"derivedFrom":[subQ0,subQ5]});Q8=makeQuery(id+"F0.imprint","IMPRINT",FACE,{"disambiguationData":[TD([[makeQuery(id+"F0.imprint","IMPRINT",EDGE,{"disambiguationData":[TD([[subQ6,-1.0]])],"derivedFrom":subQ5}),-1.0]])]});}
            var Q9;
            {var subQ3=sQuery(id+"F0.wireOp",EDGE,"E26");var subQ5=sQuery(id+"F0.wireOp",EDGE,"E25");var subQ7=makeQuery(id+"F0.imprint","INTERSECT",VERTEX,{"derivedFrom":[subQ5,subQ3]});Q9=makeQuery(id+"F0.imprint","IMPRINT",FACE,{"disambiguationData":[TD([[makeQuery(id+"F0.imprint","IMPRINT",EDGE,{"disambiguationData":[TD([[subQ7,1.0]])],"derivedFrom":subQ5}),1.0]])]});}
            var Q10;
            {var subQ1=sQuery(id+"F0.wireOp",EDGE,"E1");var subQ3=sQuery(id+"F0.wireOp",EDGE,"E26");var subQ4=makeQuery(id+"F0.imprint","INTERSECT",VERTEX,{"derivedFrom":[subQ1,subQ3]});Q10=makeQuery(id+"F0.imprint","IMPRINT",FACE,{"disambiguationData":[TD([[makeQuery(id+"F0.imprint","IMPRINT",EDGE,{"disambiguationData":[TD([[subQ4,1.0]])],"derivedFrom":subQ3}),-1.0]])]});}
            var Q11;
            {var subQ0=sQuery(id+"F0.wireOp",EDGE,"E26");var subQ3=sQuery(id+"F0.wireOp",EDGE,"E1");var subQ4=makeQuery(id+"F0.imprint","INTERSECT",VERTEX,{"derivedFrom":[subQ3,subQ0]});Q11=makeQuery(id+"F0.imprint","IMPRINT",FACE,{"disambiguationData":[TD([[makeQuery(id+"F0.imprint","IMPRINT",EDGE,{"disambiguationData":[TD([[subQ4,-1.0]])],"derivedFrom":subQ3}),-1.0]])]});}
            var Q12;
            {var subQ3=sQuery(id+"F0.wireOp",EDGE,"E27");var subQ5=sQuery(id+"F0.wireOp",EDGE,"E25");var subQ7=makeQuery(id+"F0.imprint","INTERSECT",VERTEX,{"derivedFrom":[subQ5,subQ3]});Q12=makeQuery(id+"F0.imprint","IMPRINT",FACE,{"disambiguationData":[TD([[makeQuery(id+"F0.imprint","IMPRINT",EDGE,{"disambiguationData":[TD([[subQ7,-1.0]])],"derivedFrom":subQ5}),1.0]])]});}
            var Q13;
            {var subQ1=sQuery(id+"F0.wireOp",EDGE,"E1");var subQ3=sQuery(id+"F0.wireOp",EDGE,"E27");var subQ4=makeQuery(id+"F0.imprint","INTERSECT",VERTEX,{"derivedFrom":[subQ1,subQ3]});Q13=makeQuery(id+"F0.imprint","IMPRINT",FACE,{"disambiguationData":[TD([[makeQuery(id+"F0.imprint","IMPRINT",EDGE,{"disambiguationData":[TD([[subQ4,1.0]])],"derivedFrom":subQ3}),1.0]])]});}
            var Q14;
            {var subQ3=sQuery(id+"F0.wireOp",EDGE,"E28");var subQ5=sQuery(id+"F0.wireOp",EDGE,"E1");var subQ6=makeQuery(id+"F0.imprint","INTERSECT",VERTEX,{"derivedFrom":[subQ5,subQ3]});Q14=makeQuery(id+"F0.imprint","IMPRINT",FACE,{"disambiguationData":[TD([[makeQuery(id+"F0.imprint","IMPRINT",EDGE,{"disambiguationData":[TD([[subQ6,-1.0]])],"derivedFrom":subQ5}),1.0]])]});}
            var Q15;
            {var subQ0=sQuery(id+"F0.wireOp",EDGE,"E28");var subQ1=sQuery(id+"F0.wireOp",EDGE,"E1");var subQ2=makeQuery(id+"F0.imprint","INTERSECT",VERTEX,{"derivedFrom":[subQ1,subQ0]});Q15=makeQuery(id+"F0.imprint","IMPRINT",FACE,{"disambiguationData":[TD([[makeQuery(id+"F0.imprint","IMPRINT",EDGE,{"disambiguationData":[TD([[subQ2,-1.0]])],"derivedFrom":subQ1}),-1.0]])]});}
            var Q16;
            {var subQ0=sQuery(id+"F0.wireOp",EDGE,"E25");var subQ4=sQuery(id+"F0.wireOp",EDGE,"E22");var subQ5=makeQuery(id+"F0.imprint","INTERSECT",VERTEX,{"derivedFrom":[subQ4,subQ0]});Q16=makeQuery(id+"F0.imprint","IMPRINT",FACE,{"disambiguationData":[TD([[makeQuery(id+"F0.imprint","IMPRINT",EDGE,{"disambiguationData":[TD([[subQ5,-1.0]])],"derivedFrom":subQ4}),1.0]])]});}
            var Q17;
            {var subQ1=sQuery(id+"F0.wireOp",EDGE,"E17");var subQ3=sQuery(id+"F0.wireOp",EDGE,"E21");var subQ4=makeQuery(id+"F0.imprint","INTERSECT",VERTEX,{"derivedFrom":[subQ1,subQ3]});Q17=makeQuery(id+"F0.imprint","IMPRINT",FACE,{"disambiguationData":[TD([[makeQuery(id+"F0.imprint","IMPRINT",EDGE,{"disambiguationData":[TD([[subQ4,1.0]])],"derivedFrom":subQ3}),1.0]])]});}
            var Q18;
            {var subQ0=sQuery(id+"F0.wireOp",EDGE,"E31");var subQ1=sQuery(id+"F0.wireOp",EDGE,"E1");var subQ2=makeQuery(id+"F0.imprint","INTERSECT",VERTEX,{"disambiguationData":[OD(1.0)],"derivedFrom":[subQ1,subQ0]});Q18=makeQuery(id+"F0.imprint","IMPRINT",FACE,{"disambiguationData":[TD([[makeQuery(id+"F0.imprint","IMPRINT",EDGE,{"disambiguationData":[TD([[subQ2,-1.0]])],"derivedFrom":subQ1}),1.0]])]});}
            var Q19;
            {var subQ0=sQuery(id+"F0.wireOp",EDGE,"E31");var subQ1=sQuery(id+"F0.wireOp",EDGE,"E1");var subQ2=makeQuery(id+"F0.imprint","INTERSECT",VERTEX,{"disambiguationData":[OD(0.0)],"derivedFrom":[subQ1,subQ0]});Q19=makeQuery(id+"F0.imprint","IMPRINT",FACE,{"disambiguationData":[TD([[makeQuery(id+"F0.imprint","IMPRINT",EDGE,{"disambiguationData":[TD([[subQ2,-1.0]])],"derivedFrom":subQ1}),1.0]])]});}
            var Q20;
            {var subQ1=sQuery(id+"F0.wireOp",EDGE,"E1");var subQ5=sQuery(id+"F0.wireOp",EDGE,"E31");var subQ9=makeQuery(id+"F0.imprint","INTERSECT",VERTEX,{"disambiguationData":[OD(0.0)],"derivedFrom":[subQ1,subQ5]});Q20=makeQuery(id+"F0.imprint","IMPRINT",FACE,{"disambiguationData":[TD([[makeQuery(id+"F0.imprint","IMPRINT",EDGE,{"disambiguationData":[TD([[subQ9,-1.0]])],"derivedFrom":subQ1}),-1.0]])]});}
            var Q21;
            {var subQ0=sQuery(id+"F0.wireOp",EDGE,"E17");var subQ5=sQuery(id+"F0.wireOp",EDGE,"E21");var subQ6=makeQuery(id+"F0.imprint","INTERSECT",VERTEX,{"derivedFrom":[subQ0,subQ5]});Q21=makeQuery(id+"F0.imprint","IMPRINT",FACE,{"disambiguationData":[TD([[makeQuery(id+"F0.imprint","IMPRINT",EDGE,{"disambiguationData":[TD([[subQ6,1.0]])],"derivedFrom":subQ5}),-1.0]])]});}
            var Q22;
            {var subQ0=sQuery(id+"F0.wireOp",EDGE,"E31");var subQ1=sQuery(id+"F0.wireOp",EDGE,"E1");var subQ2=makeQuery(id+"F0.imprint","INTERSECT",VERTEX,{"disambiguationData":[OD(1.0)],"derivedFrom":[subQ1,subQ0]});Q22=makeQuery(id+"F0.imprint","IMPRINT",FACE,{"disambiguationData":[TD([[makeQuery(id+"F0.imprint","IMPRINT",EDGE,{"disambiguationData":[TD([[subQ2,-1.0]])],"derivedFrom":subQ1}),-1.0]])]});}
            extrude(context, id + "F17", {"entities" : qUnion([Q0, Q1, Q2, Q3, Q4, Q5, Q6, Q7, Q8, Q9, Q10, Q11, Q12, Q13, Q14, Q15, Q16, Q17, Q18, Q19, Q20, Q21, Q22]), "depth" : 22 * mm});
        }
        {
            var Q0;
            {var subQ5=sQuery(id+"F4.wireOp",EDGE,"E147");Q0=makeQuery(id+"F4.imprint","IMPRINT",FACE,{"disambiguationData":[TD([[makeQuery(id+"F4.imprint","IMPRINT",EDGE,{"derivedFrom":subQ5}),1.0]])]});}
            var Q1;
            {var subQ0=sQuery(id+"F4.wireOp",EDGE,"E151");var subQ1=sQuery(id+"F4.wireOp",EDGE,"E137");var subQ2=makeQuery(id+"F4.imprint","INTERSECT",VERTEX,{"derivedFrom":[subQ1,subQ0]});Q1=makeQuery(id+"F4.imprint","IMPRINT",FACE,{"disambiguationData":[TD([[makeQuery(id+"F4.imprint","IMPRINT",EDGE,{"disambiguationData":[TD([[subQ2,-1.0]])],"derivedFrom":subQ1}),1.0]])]});}
            var Q2;
            {var subQ0=sQuery(id+"F4.wireOp",EDGE,"E153");var subQ1=sQuery(id+"F4.wireOp",EDGE,"E138");var subQ2=makeQuery(id+"F4.imprint","INTERSECT",VERTEX,{"derivedFrom":[subQ1,subQ0]});Q2=makeQuery(id+"F4.imprint","IMPRINT",FACE,{"disambiguationData":[TD([[makeQuery(id+"F4.imprint","IMPRINT",EDGE,{"disambiguationData":[TD([[subQ2,-1.0]])],"derivedFrom":subQ1}),-1.0]])]});}
            var Q3;
            {var subQ5=sQuery(id+"F4.wireOp",EDGE,"E146");Q3=makeQuery(id+"F4.imprint","IMPRINT",FACE,{"disambiguationData":[TD([[makeQuery(id+"F4.imprint","IMPRINT",EDGE,{"derivedFrom":subQ5}),-1.0]])]});}
            extrude(context, id + "F18", {"entities" : qUnion([Q0, Q1, Q2, Q3]), "operationType" : NewBodyOperationType.REMOVE, "oppositeDirection" : true, "depth" : 12 * mm});
        }
        {
            var Q0;
            Q0=qCreatedBy(makeId("Front.planeOp"),FACE);
            var sketch = newSketch(context, id + "F19", { "sketchPlane" : qUnion([Q0])});
            skCircle(sketch, "E161", {"center": v(-74, 0) * mm, "radius": 8 * mm});
            skLineSegment(sketch, "E162", {"start": v(0, 0) * mm, "end": v(0, -50) * mm});
            skLineSegment(sketch, "E163", {"start": v(0, -50) * mm, "end": v(0, 50) * mm});
            skLineSegment(sketch, "E164", {"start": v(-74, 0) * mm, "end": v(0, 0) * mm});
            skSolve(sketch);
        }
        {
            var Q0;
            Q0=makeQuery(id+"F19.imprint","IMPRINT",FACE,{"disambiguationData":[TD([[makeQuery(id+"F19.imprint","IMPRINT",EDGE,{"derivedFrom":sQuery(id+"F19.wireOp",EDGE,"E161")}),1.0]])]});
            var Q1;
            Q1=sQuery(id+"F19.wireOp",EDGE,"E163");
            revolve(context, id + "F20", {"operationType" : NewBodyOperationType.REMOVE, "entities" : qUnion([Q0]), "axis" : qUnion([Q1]), "revolveType" : RevolveType.FULL, "oppositeDirection" : true});
        }
        {
            var Q0;
            Q0=makeQuery(id+"F17.opExtrude","CAP_EDGE",EDGE,{"disambiguationData":[OSD([sQuery(id+"F0.wireOp",EDGE,"E18"),sQuery(id+"F0.wireOp",EDGE,"E19"),sQuery(id+"F0.wireOp",EDGE,"E20")])],"isStart":false});
            fillet(context, id + "F21", {"entities" : qUnion([Q0]), "radius" : 9 * mm, "tangentPropagation" : true, "allowEdgeOverflow" : false});
        }
        {
            var Q0;
            {var subQ0=sQuery(id+"F0.wireOp",EDGE,"E17");var subQ5=sQuery(id+"F0.wireOp",EDGE,"E21");var subQ6=makeQuery(id+"F0.imprint","INTERSECT",VERTEX,{"derivedFrom":[subQ0,subQ5]});Q0=makeQuery(id+"F0.imprint","IMPRINT",FACE,{"disambiguationData":[TD([[makeQuery(id+"F0.imprint","IMPRINT",EDGE,{"disambiguationData":[TD([[subQ6,1.0]])],"derivedFrom":subQ5}),-1.0]])]});}
            var Q1;
            {var subQ0=sQuery(id+"F0.wireOp",EDGE,"E15");var subQ5=sQuery(id+"F0.wireOp",EDGE,"E21");var subQ7=makeQuery(id+"F0.imprint","INTERSECT",VERTEX,{"derivedFrom":[subQ0,subQ5]});Q1=makeQuery(id+"F0.imprint","IMPRINT",FACE,{"disambiguationData":[TD([[makeQuery(id+"F0.imprint","IMPRINT",EDGE,{"disambiguationData":[TD([[subQ7,-1.0]])],"derivedFrom":subQ5}),-1.0]])]});}
            var Q2;
            {var subQ0=sQuery(id+"F0.wireOp",EDGE,"E31");var subQ1=sQuery(id+"F0.wireOp",EDGE,"E1");var subQ2=makeQuery(id+"F0.imprint","INTERSECT",VERTEX,{"disambiguationData":[OD(1.0)],"derivedFrom":[subQ1,subQ0]});Q2=makeQuery(id+"F0.imprint","IMPRINT",FACE,{"disambiguationData":[TD([[makeQuery(id+"F0.imprint","IMPRINT",EDGE,{"disambiguationData":[TD([[subQ2,-1.0]])],"derivedFrom":subQ1}),1.0]])]});}
            var Q3;
            {var subQ5=sQuery(id+"F0.wireOp",EDGE,"E26");var subQ7=sQuery(id+"F0.wireOp",EDGE,"E1");var subQ8=makeQuery(id+"F0.imprint","INTERSECT",VERTEX,{"derivedFrom":[subQ7,subQ5]});Q3=makeQuery(id+"F0.imprint","IMPRINT",FACE,{"disambiguationData":[TD([[makeQuery(id+"F0.imprint","IMPRINT",EDGE,{"disambiguationData":[TD([[subQ8,-1.0]])],"derivedFrom":subQ7}),1.0]])]});}
            var Q4;
            {var subQ0=sQuery(id+"F0.wireOp",EDGE,"E31");var subQ1=sQuery(id+"F0.wireOp",EDGE,"E1");var subQ2=makeQuery(id+"F0.imprint","INTERSECT",VERTEX,{"disambiguationData":[OD(0.0)],"derivedFrom":[subQ1,subQ0]});Q4=makeQuery(id+"F0.imprint","IMPRINT",FACE,{"disambiguationData":[TD([[makeQuery(id+"F0.imprint","IMPRINT",EDGE,{"disambiguationData":[TD([[subQ2,-1.0]])],"derivedFrom":subQ1}),1.0]])]});}
            var Q5;
            {var subQ0=sQuery(id+"F0.wireOp",EDGE,"E28");var subQ1=sQuery(id+"F0.wireOp",EDGE,"E1");var subQ2=makeQuery(id+"F0.imprint","INTERSECT",VERTEX,{"derivedFrom":[subQ1,subQ0]});Q5=makeQuery(id+"F0.imprint","IMPRINT",FACE,{"disambiguationData":[TD([[makeQuery(id+"F0.imprint","IMPRINT",EDGE,{"disambiguationData":[TD([[subQ2,-1.0]])],"derivedFrom":subQ1}),1.0]])]});}
            extrude(context, id + "F22", {"entities" : qUnion([Q0, Q1, Q2, Q3, Q4, Q5]), "operationType" : NewBodyOperationType.REMOVE, "depth" : 17.5 * mm});
        }
        {
            var Q0;
            Q0=qCreatedBy(makeId("Front.planeOp"),FACE);
            var sketch = newSketch(context, id + "F23", { "sketchPlane" : qUnion([Q0])});
            skLineSegment(sketch, "E165", {"start": v(0, 0) * mm, "end": v(-45, 0) * mm});
            skCircle(sketch, "E166", {"center": v(-45, 0) * mm, "radius": 3 * mm});
            skLineSegment(sketch, "E167", {"start": v(0, 0) * mm, "end": v(45, 0) * mm});
            skCircle(sketch, "E168", {"center": v(45, 0) * mm, "radius": 3 * mm});
            skSolve(sketch);
        }
        {
            var Q0;
            Q0=makeQuery(id+"F23.imprint","IMPRINT",FACE,{"disambiguationData":[TD([[makeQuery(id+"F23.imprint","IMPRINT",EDGE,{"derivedFrom":sQuery(id+"F23.wireOp",EDGE,"E166")}),1.0]])]});
            extrude(context, id + "F24", {"entities" : qUnion([Q0]), "operationType" : NewBodyOperationType.REMOVE, "depth" : 100 * mm, "hasSecondDirection" : true, "secondDirectionOppositeDirection" : false, "secondDirectionDepth" : 65 * mm});
        }
        {
            var Q0;
            Q0=makeQuery(id+"F17.opExtrude","CAP_FACE",FACE,{"disambiguationData":[OSD([sQuery(id+"F0.wireOp",EDGE,"E5"),sQuery(id+"F0.wireOp",EDGE,"E8"),sQuery(id+"F0.wireOp",EDGE,"E14"),sQuery(id+"F0.wireOp",EDGE,"E16"),sQuery(id+"F0.wireOp",EDGE,"E18"),sQuery(id+"F0.wireOp",EDGE,"E19"),sQuery(id+"F0.wireOp",EDGE,"E20"),sQuery(id+"F0.wireOp",EDGE,"E22"),sQuery(id+"F0.wireOp",EDGE,"E23"),sQuery(id+"F0.wireOp",EDGE,"E24")])],"isStart":false});
            cPlane(context, id + "F25", {"entities" : qUnion([Q0]), "cplaneType" : CPlaneType.OFFSET, "offset" : 0 * mm, "width" : 150 * mm, "height" : 150 * mm});
        }
        {
            var Q0;
            Q0=qCreatedBy(id+"F25.planeOp",FACE);
            var sketch = newSketch(context, id + "F26", { "sketchPlane" : qUnion([Q0])});
            skLineSegment(sketch, "E169", {"start": v(0, 0) * mm, "end": v(0, -40) * mm});
            skLineSegment(sketch, "E170", {"start": v(0, -40) * mm, "end": v(40, -40) * mm});
            skLineSegment(sketch, "E171", {"start": v(0, -40) * mm, "end": v(-40, -40) * mm});
            skLineSegment(sketch, "E172.0", {"start": v(-44.93, -37) * mm, "end": v(-39.87, -34.23) * mm});
            skLineSegment(sketch, "E172.1", {"start": v(-39.87, -34.23) * mm, "end": v(-34.93, -37.23) * mm});
            skLineSegment(sketch, "E172.2", {"start": v(-34.93, -37.23) * mm, "end": v(-35.07, -43) * mm});
            skLineSegment(sketch, "E172.3", {"start": v(-35.07, -43) * mm, "end": v(-40.13, -45.77) * mm});
            skLineSegment(sketch, "E172.4", {"start": v(-40.13, -45.77) * mm, "end": v(-45.07, -42.77) * mm});
            skLineSegment(sketch, "E172.5", {"start": v(-45.07, -42.77) * mm, "end": v(-44.93, -37) * mm});
            skPoint(sketch, "E172.0.midPoint", {"position": v(-42.4, -35.61) * mm});
            skLineSegment(sketch, "E173.0", {"start": v(40.16, -34.23) * mm, "end": v(45.08, -37.25) * mm});
            skLineSegment(sketch, "E173.1", {"start": v(45.08, -37.25) * mm, "end": v(44.92, -43.02) * mm});
            skLineSegment(sketch, "E173.2", {"start": v(44.92, -43.02) * mm, "end": v(39.84, -45.77) * mm});
            skLineSegment(sketch, "E173.3", {"start": v(39.84, -45.77) * mm, "end": v(34.92, -42.75) * mm});
            skLineSegment(sketch, "E173.4", {"start": v(34.92, -42.75) * mm, "end": v(35.08, -36.98) * mm});
            skLineSegment(sketch, "E173.5", {"start": v(35.08, -36.98) * mm, "end": v(40.16, -34.23) * mm});
            skPoint(sketch, "E173.0.midPoint", {"position": v(42.62, -35.74) * mm});
            skLineSegment(sketch, "E174", {"start": v(0, 0) * mm, "end": v(0, -94) * mm});
            skLineSegment(sketch, "E175.0", {"start": v(-2.89, -89) * mm, "end": v(2.89, -89) * mm});
            skLineSegment(sketch, "E175.1", {"start": v(2.89, -89) * mm, "end": v(5.77, -94) * mm});
            skLineSegment(sketch, "E175.2", {"start": v(5.77, -94) * mm, "end": v(2.89, -99) * mm});
            skLineSegment(sketch, "E175.3", {"start": v(2.89, -99) * mm, "end": v(-2.89, -99) * mm});
            skLineSegment(sketch, "E175.4", {"start": v(-2.89, -99) * mm, "end": v(-5.77, -94) * mm});
            skLineSegment(sketch, "E175.5", {"start": v(-5.77, -94) * mm, "end": v(-2.89, -89) * mm});
            skPoint(sketch, "E175.0.midPoint", {"position": v(0, -89) * mm});
            skSolve(sketch);
        }
        {
            var Q0;
            Q0=makeQuery(id+"F26.imprint","IMPRINT",FACE,{"disambiguationData":[TD([[makeQuery(id+"F26.imprint","IMPRINT",EDGE,{"derivedFrom":sQuery(id+"F26.wireOp",EDGE,"E172.0")}),-1.0]])]});
            var Q1;
            Q1=makeQuery(id+"F26.imprint","IMPRINT",FACE,{"disambiguationData":[TD([[makeQuery(id+"F26.imprint","IMPRINT",EDGE,{"derivedFrom":sQuery(id+"F26.wireOp",EDGE,"E173.0")}),-1.0]])]});
            var Q2;
            {var subQ0=sQuery(id+"F26.wireOp",EDGE,"386cfd39-7e30-42ab-8082-9fc8ef5bdbe1.1");Q2=makeQuery(id+"F26.imprint","IMPRINT",FACE,{"disambiguationData":[TD([[makeQuery(id+"F26.imprint","IMPRINT",EDGE,{"derivedFrom":subQ0}),-1.0]])]});}
            var Q3;
            {var subQ0=sQuery(id+"F26.wireOp",EDGE,"E175.1");Q3=makeQuery(id+"F26.imprint","IMPRINT",FACE,{"disambiguationData":[TD([[makeQuery(id+"F26.imprint","IMPRINT",EDGE,{"derivedFrom":subQ0}),-1.0]])]});}
            extrude(context, id + "F27", {"entities" : qUnion([Q0, Q1, Q2, Q3]), "operationType" : NewBodyOperationType.REMOVE, "oppositeDirection" : true, "depth" : 6 * mm});
        }
        {
            var Q0;
            Q0=makeQuery(id+"F9.boolean.opBoolean","INTERSECT",EDGE,{"derivedFrom":[makeQuery(id+"F1.opExtrude","SWEPT_FACE",FACE,{"disambiguationData":[OSD([sQuery(id+"F0.wireOp",EDGE,"E3")])]}),makeQuery(id+"F9.opExtrude","SWEPT_FACE",FACE,{"disambiguationData":[OSD([sQuery(id+"F8.wireOp",EDGE,"E154")])]})]});
            fillet(context, id + "F28", {"entities" : qUnion([Q0]), "radius" : 1 * mm, "tangentPropagation" : true, "allowEdgeOverflow" : false});
        }
        {
            var Q0;
            Q0=makeQuery(id+"F17.opExtrude","CAP_EDGE",EDGE,{"disambiguationData":[OSD([sQuery(id+"F0.wireOp",EDGE,"E30")])],"isStart":false});
            var Q1;
            Q1=makeQuery(id+"F17.opExtrude","SWEPT_EDGE",EDGE,{"disambiguationData":[OSD([sQuery(id+"F0.wireOp",EDGE,"E22"),sQuery(id+"F0.wireOp",EDGE,"E30")])]});
            var Q2;
            Q2=makeQuery(id+"F17.opExtrude","SWEPT_EDGE",EDGE,{"disambiguationData":[OSD([sQuery(id+"F0.wireOp",EDGE,"E24"),sQuery(id+"F0.wireOp",EDGE,"E30")])]});
            fillet(context, id + "F29", {"entities" : qUnion([Q0, Q1, Q2]), "radius" : 5 * mm, "tangentPropagation" : true, "allowEdgeOverflow" : false});
        }
    });
